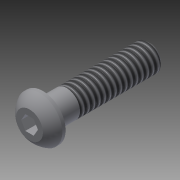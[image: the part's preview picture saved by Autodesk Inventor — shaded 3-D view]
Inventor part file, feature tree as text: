
AUTODESK INVENTOR PART (.ipt)
format: ipt  version: 2015 (Build 190159000, 159)  size: 118,784 bytes
history: native  units: in
note: dims shown in document units (in); Inventor stores cm internally (conversion verified against a paired STEP export)
features: sketch x2, revolve x1, chamfer x1, extrude x1, thread x1
ambient origin geometry x8: Origin, YZ Plane, XZ Plane, XY Plane, X Axis, Y Axis, Z Axis, Center Point
bodies: Solid1 (feature_tree)
feature tree (6):
  revolve  "Revolution1"  [1 undecoded]
  chamfer  "Chamfer1"  Distance=0.125in
  extrude  "Extrusion1"  TaperAngle=90.0deg  [1 undecoded]
  thread  "Thread1"  [1 undecoded]
  sketch  "Sketch1"  dims[d0=0.125in d1=0.211in]
  sketch  "Sketch2"  dims[d2=0.031in d3=0.125in d7=90.0deg d8=0.125in d9=0.236in d10=0.03in d11=0.125in d12=45.0deg d14=0.1562in d15=0.111in d16=0.0in d17=0.75in d18=0.0in d20=1.0in]
note: 3 required parameter values undecoded (feature->parameter linkage not recoverable at this tier; creation-order binding heuristic only, values carry confidence <= 0.55)